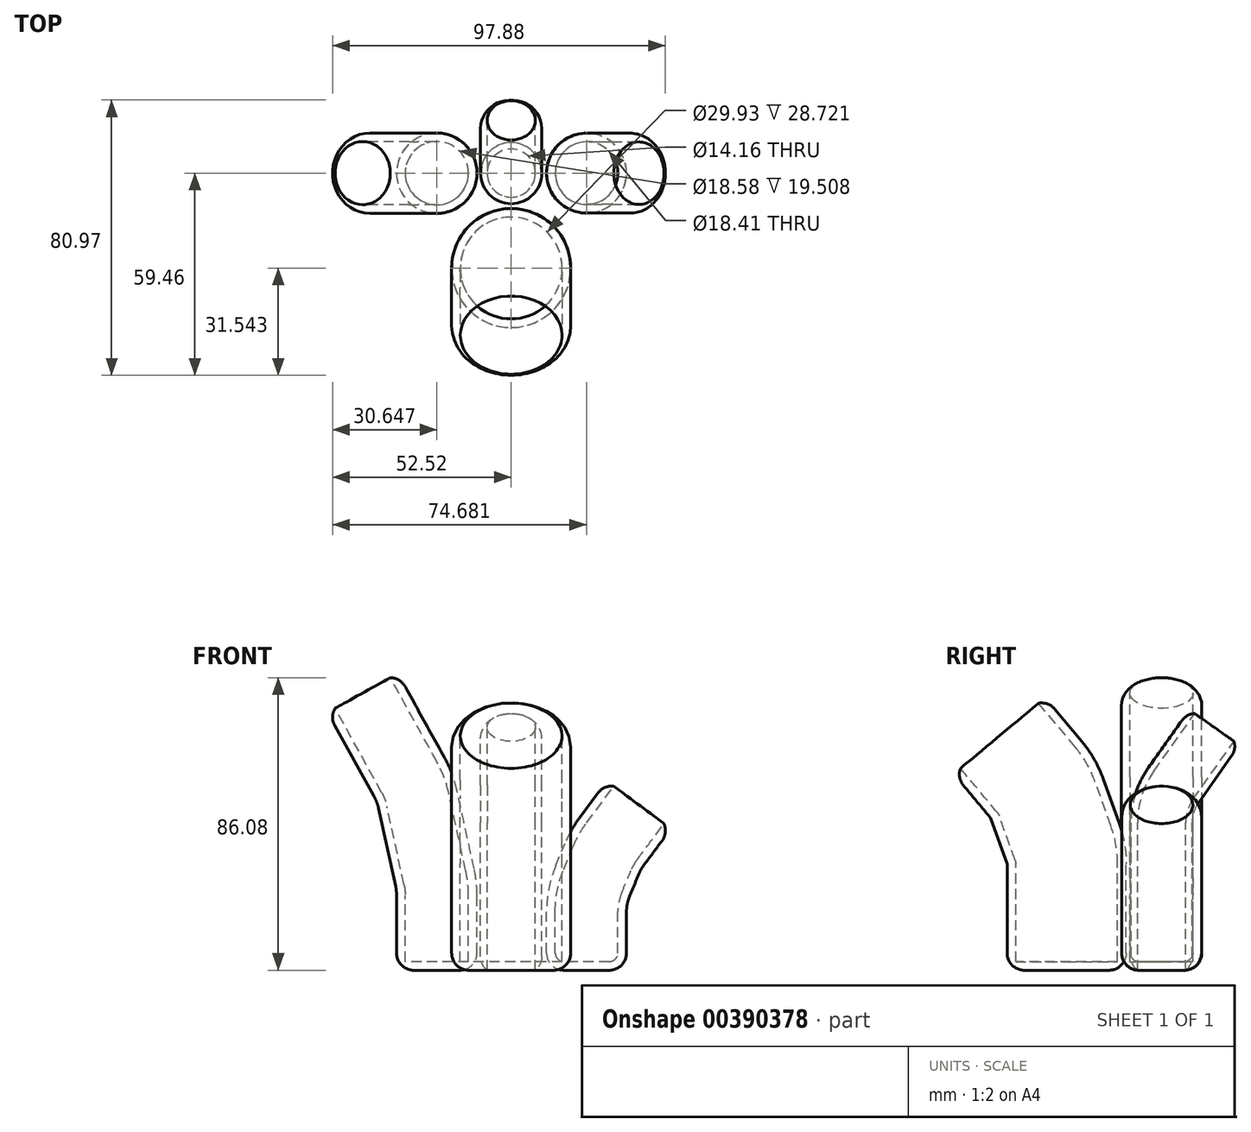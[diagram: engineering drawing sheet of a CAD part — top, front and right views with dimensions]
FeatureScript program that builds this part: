
annotation { "Feature Type Name" : "Feature", "Feature Type Description" : "" }
export const myFeature = defineFeature(function(context is Context, id is Id, definition is map)
    precondition{}
    {
        {
            var Q0;
            Q0=qCreatedBy(makeId("Right.planeOp"),FACE);
            var sketch = newSketch(context, id + "F0", { "sketchPlane" : qUnion([Q0])});
            skLineSegment(sketch, "E0", {"start": v(0, 0) * mm, "end": v(0, 43.44) * mm});
            skLineSegment(sketch, "E1", {"start": v(3.5, 54.44) * mm, "end": v(15.53, 71.45) * mm});
            skPoint(sketch, "E2.visualSharp", {"position": v(0, 49.5) * mm});
            skArc(sketch, "E2.filletArc", {"start": v(3.5, 54.44) * mm, "mid": v(0.9, 49.21) * mm, "end": v(0, 43.44) * mm});
            skSolve(sketch);
        }
        {
            var Q0;
            Q0=qCreatedBy(makeId("Top.planeOp"),FACE);
            var sketch = newSketch(context, id + "F1", { "sketchPlane" : qUnion([Q0])});
            skCircle(sketch, "E3", {"center": v(0, 0) * mm, "radius": 9 * mm});
            skCircle(sketch, "E4", {"center": v(0, 0) * mm, "radius": 7.08 * mm});
            skSolve(sketch);
        }
        {
            var Q0;
            Q0=makeQuery(id+"F1.imprint","IMPRINT",FACE,{"disambiguationData":[TD([[makeQuery(id+"F1.imprint","IMPRINT",EDGE,{"derivedFrom":sQuery(id+"F1.wireOp",EDGE,"E3")}),1.0]])]});
            var Q1;
            Q1=sQuery(id+"F0.wireOp",EDGE,"E0");
            var Q2;
            Q2=sQuery(id+"F0.wireOp",EDGE,"E2.filletArc");
            var Q3;
            Q3=sQuery(id+"F0.wireOp",EDGE,"E1");
            sweep(context, id + "F2", {"profiles" : qUnion([Q0]), "path" : qUnion([Q1, Q2, Q3])});
        }
        {
            var Q0;
            Q0=qCreatedBy(makeId("Right.planeOp"),FACE);
            var sketch = newSketch(context, id + "F3", { "sketchPlane" : qUnion([Q0])});
            skLineSegment(sketch, "E5", {"start": v(-27.13, 0) * mm, "end": v(-27.13, 31.26) * mm});
            skLineSegment(sketch, "E6", {"start": v(-28.25, 37.68) * mm, "end": v(-32.92, 50.73) * mm});
            skLineSegment(sketch, "E7", {"start": v(-36.22, 56.5) * mm, "end": v(-47.05, 69.5) * mm});
            skPoint(sketch, "E8.visualSharp", {"position": v(-34.06, 53.9) * mm});
            skArc(sketch, "E8.filletArc", {"start": v(-32.92, 50.73) * mm, "mid": v(-34.32, 53.76) * mm, "end": v(-36.22, 56.5) * mm});
            skPoint(sketch, "E9.visualSharp", {"position": v(-27.13, 34.57) * mm});
            skArc(sketch, "E9.filletArc", {"start": v(-27.13, 31.26) * mm, "mid": v(-27.41, 34.52) * mm, "end": v(-28.25, 37.68) * mm});
            skSolve(sketch);
        }
        {
            var Q0;
            Q0=qCreatedBy(makeId("Top.planeOp"),FACE);
            var sketch = newSketch(context, id + "F4", { "sketchPlane" : qUnion([Q0])});
            skCircle(sketch, "E10", {"center": v(0, -27.92) * mm, "radius": 17.5 * mm});
            skCircle(sketch, "E11", {"center": v(0, -27.92) * mm, "radius": 14.97 * mm});
            skSolve(sketch);
        }
        {
            var Q0;
            Q0=makeQuery(id+"F4.imprint","IMPRINT",FACE,{"disambiguationData":[TD([[makeQuery(id+"F4.imprint","IMPRINT",EDGE,{"derivedFrom":sQuery(id+"F4.wireOp",EDGE,"E11")}),1.0]])]});
            var Q1;
            Q1=makeQuery(id+"F4.imprint","IMPRINT",FACE,{"disambiguationData":[TD([[makeQuery(id+"F4.imprint","IMPRINT",EDGE,{"derivedFrom":sQuery(id+"F4.wireOp",EDGE,"E10")}),1.0]])]});
            var Q2;
            Q2=sQuery(id+"F3.wireOp",EDGE,"E5");
            var Q3;
            Q3=sQuery(id+"F3.wireOp",EDGE,"E9.filletArc");
            var Q4;
            Q4=sQuery(id+"F3.wireOp",EDGE,"E6");
            var Q5;
            Q5=sQuery(id+"F3.wireOp",EDGE,"E8.filletArc");
            var Q6;
            Q6=sQuery(id+"F3.wireOp",EDGE,"E7");
            sweep(context, id + "F5", {"profiles" : qUnion([Q0, Q1]), "path" : qUnion([Q2, Q3, Q4, Q5, Q6])});
        }
        {
            var Q0;
            Q0=makeQuery(id+"F5.opSweep","CAP_FACE",FACE,{"disambiguationData":[OSD([sQuery(id+"F3.wireOp",VERTEX,"E7.end"),sQuery(id+"F4.wireOp",EDGE,"E10")])],"isStart":false});
            shell(context, id + "F6", {"entities" : qUnion([Q0]), "thickness" : 2.54 * mm});
        }
        {
            var Q0;
            Q0=qCreatedBy(makeId("Front.planeOp"),FACE);
            var sketch = newSketch(context, id + "F7", { "sketchPlane" : qUnion([Q0])});
            skLineSegment(sketch, "E12", {"start": v(-20.91, 0) * mm, "end": v(-20.91, 22.05) * mm});
            skLineSegment(sketch, "E13", {"start": v(-21.5, 27.48) * mm, "end": v(-26.52, 50.42) * mm});
            skLineSegment(sketch, "E14", {"start": v(-29.12, 57.3) * mm, "end": v(-42.83, 82.04) * mm});
            skPoint(sketch, "E15.visualSharp", {"position": v(-27.31, 54.06) * mm});
            skArc(sketch, "E15.filletArc", {"start": v(-26.52, 50.42) * mm, "mid": v(-27.57, 53.96) * mm, "end": v(-29.12, 57.3) * mm});
            skPoint(sketch, "E16.visualSharp", {"position": v(-20.91, 24.8) * mm});
            skArc(sketch, "E16.filletArc", {"start": v(-20.91, 22.05) * mm, "mid": v(-21.06, 24.78) * mm, "end": v(-21.5, 27.48) * mm});
            skSolve(sketch);
        }
        {
            var Q0;
            Q0=qCreatedBy(makeId("Top.planeOp"),FACE);
            var sketch = newSketch(context, id + "F8", { "sketchPlane" : qUnion([Q0])});
            skCircle(sketch, "E17", {"center": v(-21.87, 0) * mm, "radius": 11.83 * mm});
            skCircle(sketch, "E18", {"center": v(-21.87, 0) * mm, "radius": 9.47 * mm});
            skSolve(sketch);
        }
        {
            var Q0;
            Q0=makeQuery(id+"F8.imprint","IMPRINT",FACE,{"disambiguationData":[TD([[makeQuery(id+"F8.imprint","IMPRINT",EDGE,{"derivedFrom":sQuery(id+"F8.wireOp",EDGE,"E18")}),1.0]])]});
            var Q1;
            Q1=makeQuery(id+"F8.imprint","IMPRINT",FACE,{"disambiguationData":[TD([[makeQuery(id+"F8.imprint","IMPRINT",EDGE,{"derivedFrom":sQuery(id+"F8.wireOp",EDGE,"E17")}),1.0]])]});
            var Q2;
            Q2=sQuery(id+"F7.wireOp",EDGE,"E12");
            var Q3;
            Q3=sQuery(id+"F7.wireOp",EDGE,"E16.filletArc");
            var Q4;
            Q4=sQuery(id+"F7.wireOp",EDGE,"E13");
            var Q5;
            Q5=sQuery(id+"F7.wireOp",EDGE,"E15.filletArc");
            var Q6;
            Q6=sQuery(id+"F7.wireOp",EDGE,"E14");
            sweep(context, id + "F9", {"profiles" : qUnion([Q0, Q1]), "path" : qUnion([Q2, Q3, Q4, Q5, Q6])});
        }
        {
            var Q0;
            Q0=makeQuery(id+"F9.opSweep","CAP_FACE",FACE,{"disambiguationData":[OSD([sQuery(id+"F7.wireOp",VERTEX,"E14.end"),sQuery(id+"F8.wireOp",EDGE,"E17")])],"isStart":false});
            shell(context, id + "F10", {"entities" : qUnion([Q0]), "thickness" : 2.54 * mm});
        }
        {
            var Q0;
            Q0=qCreatedBy(makeId("Front.planeOp"),FACE);
            var sketch = newSketch(context, id + "F11", { "sketchPlane" : qUnion([Q0])});
            skLineSegment(sketch, "E19", {"start": v(20.38, 0) * mm, "end": v(20.38, 17.2) * mm});
            skLineSegment(sketch, "E20", {"start": v(22.3, 26.89) * mm, "end": v(25.04, 33.5) * mm});
            skLineSegment(sketch, "E21", {"start": v(28.14, 38.98) * mm, "end": v(36.13, 49.71) * mm});
            skPoint(sketch, "E22.visualSharp", {"position": v(26.25, 36.44) * mm});
            skArc(sketch, "E22.filletArc", {"start": v(28.14, 38.98) * mm, "mid": v(26.42, 36.34) * mm, "end": v(25.04, 33.5) * mm});
            skPoint(sketch, "E23.visualSharp", {"position": v(20.38, 22.23) * mm});
            skArc(sketch, "E23.filletArc", {"start": v(22.3, 26.89) * mm, "mid": v(20.87, 22.13) * mm, "end": v(20.38, 17.2) * mm});
            skSolve(sketch);
        }
        {
            var Q0;
            Q0=qCreatedBy(makeId("Top.planeOp"),FACE);
            var sketch = newSketch(context, id + "F12", { "sketchPlane" : qUnion([Q0])});
            skCircle(sketch, "E24", {"center": v(22.16, 0) * mm, "radius": 11.75 * mm});
            skCircle(sketch, "E25", {"center": v(22.16, 0) * mm, "radius": 9.67 * mm});
            skSolve(sketch);
        }
        {
            var Q0;
            Q0=makeQuery(id+"F12.imprint","IMPRINT",FACE,{"disambiguationData":[TD([[makeQuery(id+"F12.imprint","IMPRINT",EDGE,{"derivedFrom":sQuery(id+"F12.wireOp",EDGE,"E25")}),1.0]])]});
            var Q1;
            Q1=makeQuery(id+"F12.imprint","IMPRINT",FACE,{"disambiguationData":[TD([[makeQuery(id+"F12.imprint","IMPRINT",EDGE,{"derivedFrom":sQuery(id+"F12.wireOp",EDGE,"E24")}),1.0]])]});
            var Q2;
            Q2=sQuery(id+"F11.wireOp",EDGE,"E19");
            var Q3;
            Q3=sQuery(id+"F11.wireOp",EDGE,"E23.filletArc");
            var Q4;
            Q4=sQuery(id+"F11.wireOp",EDGE,"E20");
            var Q5;
            Q5=sQuery(id+"F11.wireOp",EDGE,"E22.filletArc");
            var Q6;
            Q6=sQuery(id+"F11.wireOp",EDGE,"E21");
            sweep(context, id + "F13", {"profiles" : qUnion([Q0, Q1]), "path" : qUnion([Q2, Q3, Q4, Q5, Q6])});
        }
        {
            var Q0;
            Q0=makeQuery(id+"F13.opSweep","SWEPT_FACE",FACE,{"disambiguationData":[OSD([sQuery(id+"F11.wireOp",EDGE,"E19"),sQuery(id+"F12.wireOp",EDGE,"E24")])]});
            var Q1;
            Q1=makeQuery(id+"F2.opSweep","SWEPT_FACE",FACE,{"disambiguationData":[OSD([sQuery(id+"F0.wireOp",EDGE,"E0"),sQuery(id+"F1.wireOp",EDGE,"E3")])]});
            var Q2;
            Q2=makeQuery(id+"F9.opSweep","SWEPT_FACE",FACE,{"disambiguationData":[OSD([sQuery(id+"F7.wireOp",EDGE,"E12"),sQuery(id+"F8.wireOp",EDGE,"E17")])]});
            var Q3;
            Q3=makeQuery(id+"F13.opSweep","SWEPT_FACE",FACE,{"disambiguationData":[OSD([sQuery(id+"F11.wireOp",EDGE,"E23.filletArc"),sQuery(id+"F12.wireOp",EDGE,"E24")])]});
            var Q4;
            Q4=makeQuery(id+"F13.opSweep","SWEPT_FACE",FACE,{"disambiguationData":[OSD([sQuery(id+"F11.wireOp",EDGE,"E20"),sQuery(id+"F12.wireOp",EDGE,"E24")])]});
            var Q5;
            Q5=makeQuery(id+"F13.opSweep","SWEPT_FACE",FACE,{"disambiguationData":[OSD([sQuery(id+"F11.wireOp",EDGE,"E22.filletArc"),sQuery(id+"F12.wireOp",EDGE,"E24")])]});
            var Q6;
            Q6=makeQuery(id+"F2.opSweep","SWEPT_FACE",FACE,{"disambiguationData":[OSD([sQuery(id+"F0.wireOp",EDGE,"E2.filletArc"),sQuery(id+"F1.wireOp",EDGE,"E3")])]});
            var Q7;
            Q7=makeQuery(id+"F2.opSweep","SWEPT_FACE",FACE,{"disambiguationData":[OSD([sQuery(id+"F0.wireOp",EDGE,"E1"),sQuery(id+"F1.wireOp",EDGE,"E3")])]});
            var Q8;
            Q8=makeQuery(id+"F9.opSweep","SWEPT_FACE",FACE,{"disambiguationData":[OSD([sQuery(id+"F7.wireOp",EDGE,"E16.filletArc"),sQuery(id+"F8.wireOp",EDGE,"E17")])]});
            var Q9;
            Q9=makeQuery(id+"F9.opSweep","SWEPT_FACE",FACE,{"disambiguationData":[OSD([sQuery(id+"F7.wireOp",EDGE,"E13"),sQuery(id+"F8.wireOp",EDGE,"E17")])]});
            var Q10;
            Q10=makeQuery(id+"F9.opSweep","SWEPT_FACE",FACE,{"disambiguationData":[OSD([sQuery(id+"F7.wireOp",EDGE,"E15.filletArc"),sQuery(id+"F8.wireOp",EDGE,"E17")])]});
            var Q11;
            Q11=makeQuery(id+"F9.opSweep","SWEPT_FACE",FACE,{"disambiguationData":[OSD([sQuery(id+"F7.wireOp",EDGE,"E14"),sQuery(id+"F8.wireOp",EDGE,"E17")])]});
            var Q12;
            Q12=makeQuery(id+"F5.opSweep","SWEPT_FACE",FACE,{"disambiguationData":[OSD([sQuery(id+"F3.wireOp",EDGE,"E5"),sQuery(id+"F4.wireOp",EDGE,"E10")])]});
            var Q13;
            Q13=makeQuery(id+"F5.opSweep","SWEPT_FACE",FACE,{"disambiguationData":[OSD([sQuery(id+"F3.wireOp",EDGE,"E9.filletArc"),sQuery(id+"F4.wireOp",EDGE,"E10")])]});
            var Q14;
            Q14=makeQuery(id+"F5.opSweep","SWEPT_FACE",FACE,{"disambiguationData":[OSD([sQuery(id+"F3.wireOp",EDGE,"E6"),sQuery(id+"F4.wireOp",EDGE,"E10")])]});
            var Q15;
            Q15=makeQuery(id+"F5.opSweep","SWEPT_FACE",FACE,{"disambiguationData":[OSD([sQuery(id+"F3.wireOp",EDGE,"E8.filletArc"),sQuery(id+"F4.wireOp",EDGE,"E10")])]});
            var Q16;
            Q16=makeQuery(id+"F5.opSweep","SWEPT_FACE",FACE,{"disambiguationData":[OSD([sQuery(id+"F3.wireOp",EDGE,"E7"),sQuery(id+"F4.wireOp",EDGE,"E10")])]});
            fillet(context, id + "F14", {"entities" : qUnion([Q0, Q1, Q2, Q3, Q4, Q5, Q6, Q7, Q8, Q9, Q10, Q11, Q12, Q13, Q14, Q15, Q16]), "radius" : 5.08 * mm, "tangentPropagation" : true, "allowEdgeOverflow" : false});
        }
        {
            var Q0;
            Q0=makeQuery(id+"F13.opSweep","CAP_FACE",FACE,{"disambiguationData":[OSD([sQuery(id+"F11.wireOp",VERTEX,"E21.end"),sQuery(id+"F12.wireOp",EDGE,"E24")])],"isStart":false});
            shell(context, id + "F15", {"entities" : qUnion([Q0]), "thickness" : 2.54 * mm});
        }
        {
            var Q0;
            Q0=makeQuery(id+"F13.opSweep","SWEPT_FACE",FACE,{"disambiguationData":[OSD([sQuery(id+"F11.wireOp",EDGE,"E21"),sQuery(id+"F12.wireOp",EDGE,"E24")])]});
            fillet(context, id + "F16", {"entities" : qUnion([Q0]), "radius" : 5.08 * mm, "tangentPropagation" : true, "allowEdgeOverflow" : false});
        }
    });
